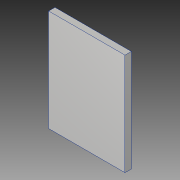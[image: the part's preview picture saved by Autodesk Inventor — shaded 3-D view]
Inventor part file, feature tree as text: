
AUTODESK INVENTOR PART (.ipt)
format: ipt  version: 2019 (Build 230136000, 136)  size: 83,968 bytes
history: native  units: in
note: dims shown in document units (in); Inventor stores cm internally (conversion verified against a paired STEP export)
features: extrude x1, sketch x1
ambient origin geometry x8: Origin, YZ Plane, XZ Plane, XY Plane, X Axis, Y Axis, Z Axis, Center Point
bodies: Solid1 (feature_tree)
feature tree (2):
  extrude  "Extrusion1"  [1 undecoded]
  sketch  "Sketch1"  dims[d3=0.0in]
note: 1 required parameter value undecoded (feature->parameter linkage not recoverable at this tier; creation-order binding heuristic only, values carry confidence <= 0.55)
